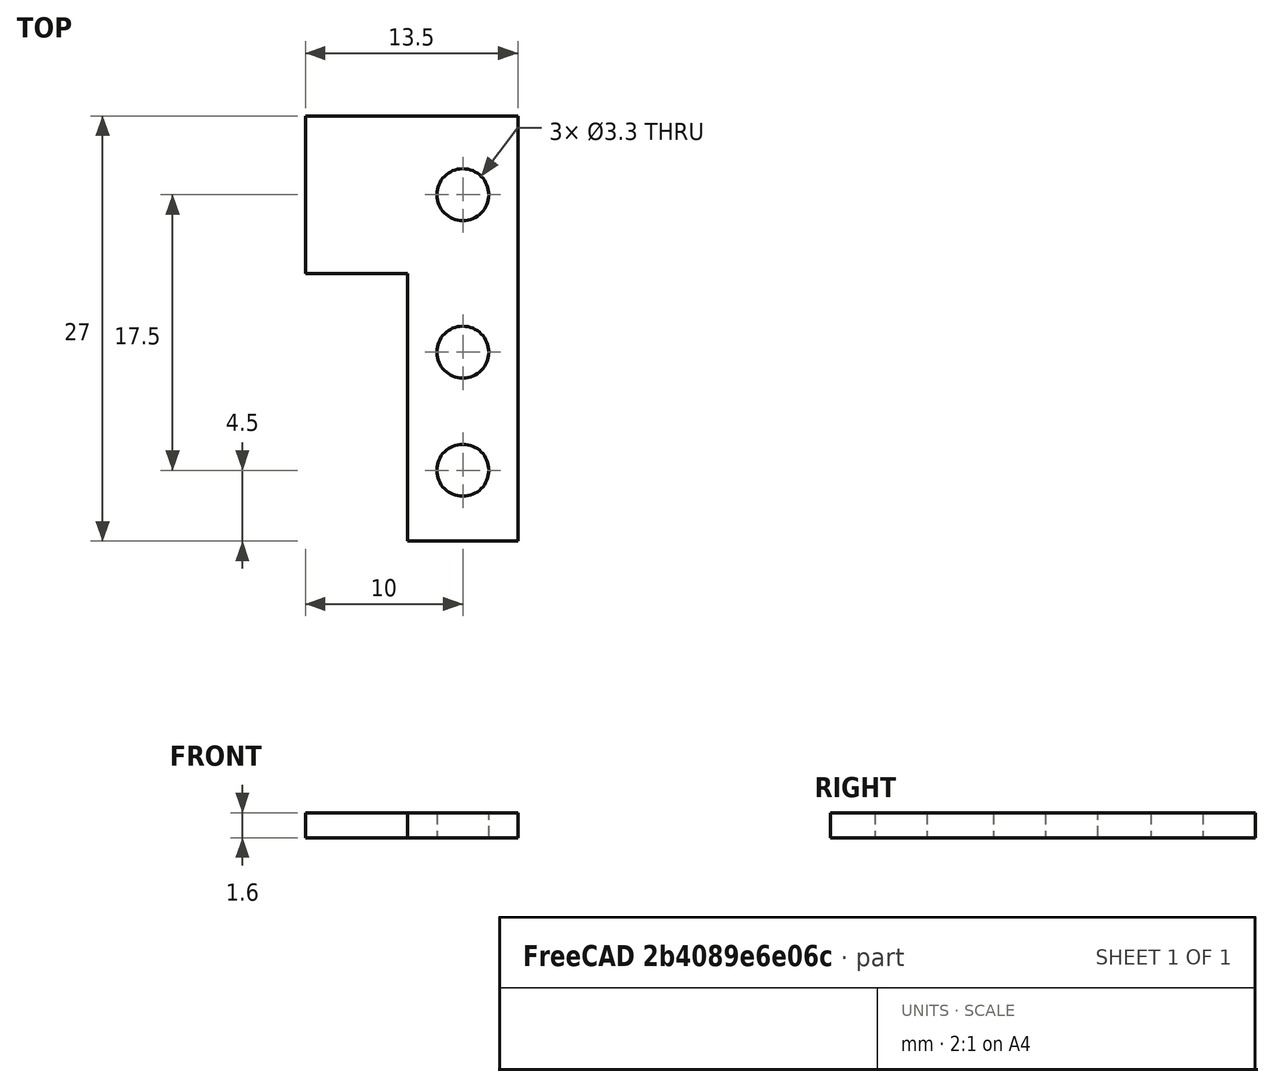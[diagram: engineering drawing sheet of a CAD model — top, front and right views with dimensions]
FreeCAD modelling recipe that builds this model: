
FCSTD DOCUMENT  (FreeCAD 0.19R24276 (Git))
Label: Pcb_support_spacer_bottom
License: All rights reserved
LicenseURL: http://en.wikipedia.org/wiki/All_rights_reserved
objects: Sketcher::SketchObject×1, PartDesign::Pad×1, PartDesign::Body×1
note: 4 computed .brp shape members not serialized (recipe doc carries the construction recipe); baked Part::Feature solids carry a one-line shape summary decoded from their .brp

FEATURE [Sketcher::SketchObject] Sketch
  FullyConstrained = true
  MapMode = 5
  Support = -> [XY_Plane]
  sketch-geometry (10):
    g0: Circle CenterX=0 CenterY=0 CenterZ=0 NormalX=0 NormalY=0 NormalZ=1 AngleXU=0 Radius=1.65
    g1: Circle CenterX=0 CenterY=-10 CenterZ=0 NormalX=0 NormalY=0 NormalZ=1 AngleXU=0 Radius=1.65
    g2: LineSegment StartX=3.5 StartY=5 StartZ=0 EndX=3.5 EndY=-22 EndZ=0
    g3: LineSegment StartX=3.5 StartY=-22 StartZ=0 EndX=-3.5 EndY=-22 EndZ=0
    g4: LineSegment StartX=-3.5 StartY=-22 StartZ=0 EndX=-3.5 EndY=-5 EndZ=0
    g5: LineSegment StartX=0 StartY=0 StartZ=0 EndX=0 EndY=-22 EndZ=0
    g6: LineSegment StartX=-10 StartY=5 StartZ=0 EndX=-10 EndY=-5 EndZ=0
    g7: LineSegment StartX=-10 StartY=-5 StartZ=0 EndX=-3.5 EndY=-5 EndZ=0
    g8: LineSegment StartX=-10 StartY=5 StartZ=0 EndX=3.5 EndY=5 EndZ=0
    g9: Circle CenterX=0 CenterY=-17.5 CenterZ=0 NormalX=0 NormalY=0 NormalZ=1 AngleXU=0 Radius=1.65
  constraints (28):
    c: Coincident(g0,g-1)
    c: PointOnObject(g1,g-2)
    c: Equal(g0,g1)
    c: Diameter(g1) = 3.3
    c: Coincident(g2,g3)
    c: Coincident(g3,g4)
    c: Horizontal(g3)
    c: Vertical(g2)
    c: Vertical(g4)
    c: Coincident(g5,g0)
    c: PointOnObject(g5,g-2)
    c: Symmetric(g3,g2,g5)
    c: DistanceX(g3,g3) = 7
    c: DistanceY(g1,g0) = 10
    c: DistanceY(g3,g1) = 12
    c: Vertical(g6)
    c: DistanceX(g6,g0) = 10
    c: Horizontal(g7)
    c: Coincident(g6,g7)
    c: Coincident(g4,g7)
    c: DistanceY(g6,g6) = 10
    c: Coincident(g8,g6)
    c: Coincident(g8,g2)
    c: Horizontal(g8)
    c: DistanceY(g0,g2) = 5
    c: PointOnObject(g9,g-2)
    c: Equal(g1,g9)
    c: DistanceY(g9,g1) = 7.5
FEATURE [PartDesign::Pad] Pad
  Direction = (1,1,1)
  Length = 1.6
  Length2 = 100
  Profile = -> Sketch
  Type = 0
FEATURE [PartDesign::Body] Body
  Group = -> [Sketch,Pad]
  Origin = -> Origin
  Tip = -> Pad
